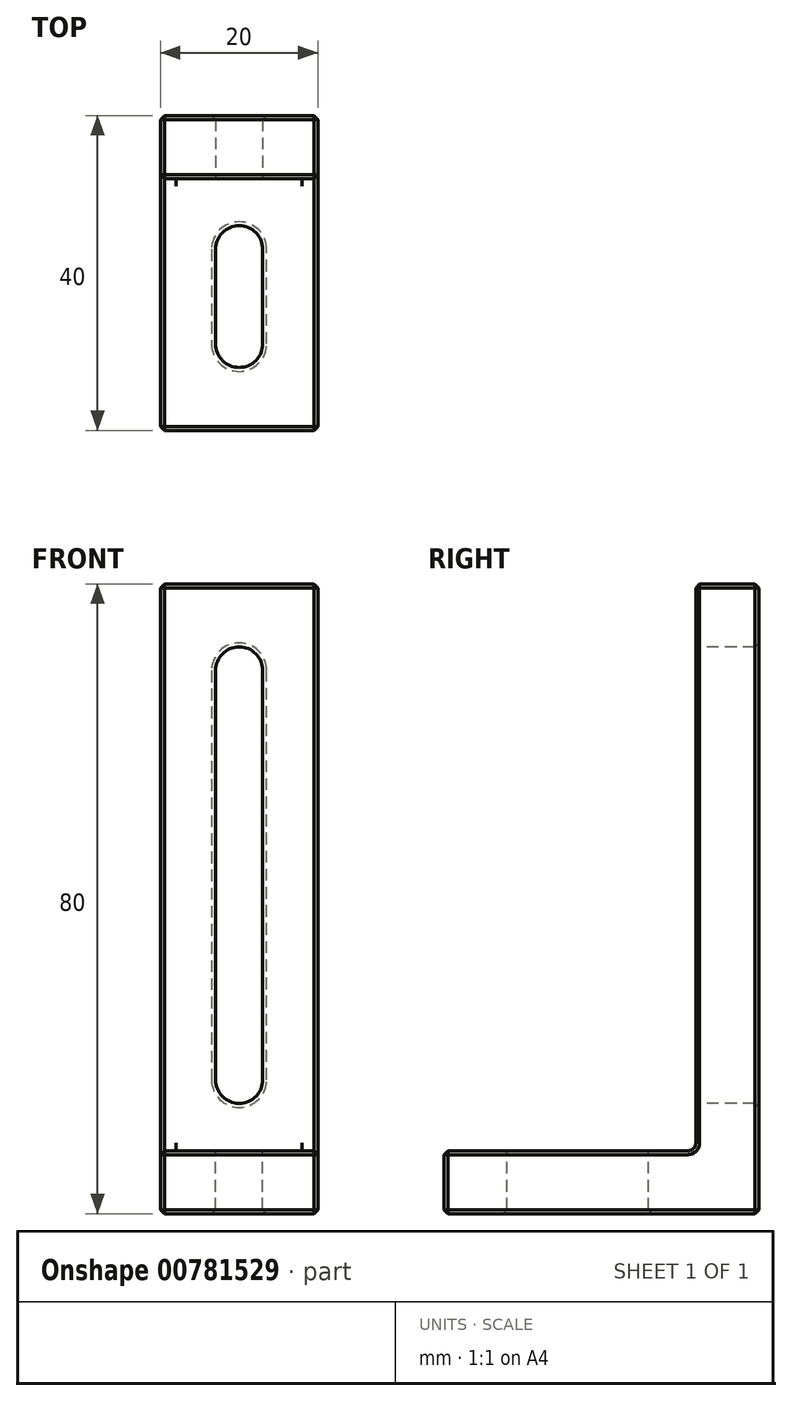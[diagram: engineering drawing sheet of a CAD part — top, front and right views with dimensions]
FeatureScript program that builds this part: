
annotation { "Feature Type Name" : "Feature", "Feature Type Description" : "" }
export const myFeature = defineFeature(function(context is Context, id is Id, definition is map)
    precondition{}
    {
        {
            var Q0;
            Q0=qCreatedBy(makeId("Right.planeOp"),FACE);
            var sketch = newSketch(context, id + "F0", { "sketchPlane" : qUnion([Q0])});
            skLineSegment(sketch, "E0", {"start": v(0, 0) * mm, "end": v(-40, 0) * mm});
            skLineSegment(sketch, "E1", {"start": v(-40, 0) * mm, "end": v(-40, 8) * mm});
            skLineSegment(sketch, "E2", {"start": v(-40, 8) * mm, "end": v(-8, 8) * mm});
            skLineSegment(sketch, "E3", {"start": v(-8, 8) * mm, "end": v(-8, 80) * mm});
            skLineSegment(sketch, "E4", {"start": v(-8, 80) * mm, "end": v(0, 80) * mm});
            skLineSegment(sketch, "E5", {"start": v(0, 80) * mm, "end": v(0, 0) * mm});
            skSolve(sketch);
        }
        {
            var Q0;
            Q0=makeQuery(id+"F0.imprint","IMPRINT",FACE,{"disambiguationData":[TD([[makeQuery(id+"F0.imprint","IMPRINT",EDGE,{"derivedFrom":sQuery(id+"F0.wireOp",EDGE,"E0")}),-1.0]])]});
            extrude(context, id + "F1", {"entities" : qUnion([Q0]), "depth" : 20 * mm, "offsetDistance" : 25 * mm});
        }
        {
            var Q0;
            Q0=makeQuery(id+"F1.opExtrude","SWEPT_EDGE",EDGE,{"disambiguationData":[OSD([sQuery(id+"F0.wireOp",EDGE,"E2"),sQuery(id+"F0.wireOp",EDGE,"E3")])]});
            fillet(context, id + "F2", {"entities" : qUnion([Q0]), "radius" : 1 * mm, "tangentPropagation" : true, "allowEdgeOverflow" : false});
        }
        {
            var Q0;
            Q0=makeQuery(id+"F1.opExtrude","SWEPT_FACE",FACE,{"disambiguationData":[OSD([sQuery(id+"F0.wireOp",EDGE,"E2")])]});
            var sketch = newSketch(context, id + "F3", { "sketchPlane" : qUnion([Q0])});
            skLineSegment(sketch, "E6.bottom", {"start": v(18, -9) * mm, "end": v(2, -9) * mm});
            skLineSegment(sketch, "E6.top", {"start": v(18, -8) * mm, "end": v(2, -8) * mm});
            skLineSegment(sketch, "E6.left", {"start": v(18, -9) * mm, "end": v(18, -8) * mm});
            skLineSegment(sketch, "E6.right", {"start": v(2, -9) * mm, "end": v(2, -8) * mm});
            skSolve(sketch);
        }
        {
            var Q0;
            Q0 = qSketchRegion(id + "F3", true);
            extrude(context, id + "F4", {"entities" : qUnion([Q0]), "operationType" : NewBodyOperationType.REMOVE, "depth" : 25 * mm, "offsetDistance" : 25 * mm});
        }
        {
            var Q0;
            Q0=makeQuery(id+"F4.boolean.opBoolean","MERGE",FACE,{"derivedFrom":[makeQuery(id+"F1.opExtrude","SWEPT_FACE",FACE,{"disambiguationData":[OSD([sQuery(id+"F0.wireOp",EDGE,"E2")])]}),makeQuery(id+"F4.opExtrude","CAP_FACE",FACE,{"disambiguationData":[OSD([sQuery(id+"F3.wireOp",EDGE,"E6.bottom"),sQuery(id+"F3.wireOp",EDGE,"E6.top"),sQuery(id+"F3.wireOp",EDGE,"E6.left"),sQuery(id+"F3.wireOp",EDGE,"E6.right")])],"isStart":true})]});
            var sketch = newSketch(context, id + "F5", { "sketchPlane" : qUnion([Q0])});
            skLineSegment(sketch, "E7", {"start": v(10, 0) * mm, "end": v(10, -40) * mm, "construction": true});
            skArc(sketch, "E8", {"start": v(7, -29) * mm, "mid": v(10, -32) * mm, "end": v(13, -29) * mm});
            skArc(sketch, "E9", {"start": v(13, -17) * mm, "mid": v(10, -14) * mm, "end": v(7, -17) * mm});
            skLineSegment(sketch, "E10", {"start": v(13, -17) * mm, "end": v(13, -29) * mm});
            skLineSegment(sketch, "E11", {"start": v(7, -17) * mm, "end": v(7, -29) * mm});
            skSolve(sketch);
        }
        {
            var Q0;
            Q0 = qSketchRegion(id + "F5", true);
            extrude(context, id + "F6", {"entities" : qUnion([Q0]), "operationType" : NewBodyOperationType.REMOVE, "oppositeDirection" : true, "depth" : 25 * mm, "offsetDistance" : 25 * mm});
        }
        {
            var Q0;
            Q0=makeQuery(id+"F4.boolean.opBoolean","MERGE",FACE,{"derivedFrom":[makeQuery(id+"F1.opExtrude","SWEPT_FACE",FACE,{"disambiguationData":[OSD([sQuery(id+"F0.wireOp",EDGE,"E3")])]}),makeQuery(id+"F4.opExtrude","SWEPT_FACE",FACE,{"disambiguationData":[OSD([sQuery(id+"F3.wireOp",EDGE,"E6.top")])]})]});
            var sketch = newSketch(context, id + "F7", { "sketchPlane" : qUnion([Q0])});
            skLineSegment(sketch, "E12", {"start": v(10, 80) * mm, "end": v(10, 0) * mm});
            skLineSegment(sketch, "E13", {"start": v(13, 69) * mm, "end": v(13, 17) * mm});
            skLineSegment(sketch, "E14", {"start": v(7, 69) * mm, "end": v(7, 17) * mm});
            skArc(sketch, "E15", {"start": v(7, 17) * mm, "mid": v(10, 14) * mm, "end": v(13, 17) * mm});
            skArc(sketch, "E16", {"start": v(13, 69) * mm, "mid": v(10, 72) * mm, "end": v(7, 69) * mm});
            skSolve(sketch);
        }
        {
            var Q0;
            Q0 = qSketchRegion(id + "F7", true);
            extrude(context, id + "F8", {"entities" : qUnion([Q0]), "operationType" : NewBodyOperationType.REMOVE, "oppositeDirection" : true, "depth" : 25 * mm, "offsetDistance" : 25 * mm});
        }
        {
            var Q0;
            Q0=makeQuery(id+"F1.opExtrude","SWEPT_FACE",FACE,{"disambiguationData":[OSD([sQuery(id+"F0.wireOp",EDGE,"E4")])]});
            var Q1;
            Q1=makeQuery(id+"F1.opExtrude","SWEPT_FACE",FACE,{"disambiguationData":[OSD([sQuery(id+"F0.wireOp",EDGE,"E1")])]});
            var Q2;
            Q2=makeQuery(id+"F1.opExtrude","CAP_FACE",FACE,{"disambiguationData":[OSD([sQuery(id+"F0.wireOp",EDGE,"E0"),sQuery(id+"F0.wireOp",EDGE,"E1"),sQuery(id+"F0.wireOp",EDGE,"E2"),sQuery(id+"F0.wireOp",EDGE,"E3"),sQuery(id+"F0.wireOp",EDGE,"E4"),sQuery(id+"F0.wireOp",EDGE,"E5")])],"isStart":false});
            var Q3;
            Q3=makeQuery(id+"F1.opExtrude","CAP_FACE",FACE,{"disambiguationData":[OSD([sQuery(id+"F0.wireOp",EDGE,"E0"),sQuery(id+"F0.wireOp",EDGE,"E1"),sQuery(id+"F0.wireOp",EDGE,"E2"),sQuery(id+"F0.wireOp",EDGE,"E3"),sQuery(id+"F0.wireOp",EDGE,"E4"),sQuery(id+"F0.wireOp",EDGE,"E5")])],"isStart":true});
            var Q4;
            Q4=makeQuery(id+"F8.boolean.opBoolean","COPY",EDGE,{"derivedFrom":makeQuery(id+"F8.opExtrude","CAP_EDGE",EDGE,{"disambiguationData":[OSD([sQuery(id+"F7.wireOp",EDGE,"E14")])],"isStart":true})});
            var Q5;
            Q5=makeQuery(id+"F8.boolean.opBoolean","INTERSECT",EDGE,{"derivedFrom":[makeQuery(id+"F1.opExtrude","SWEPT_FACE",FACE,{"disambiguationData":[OSD([sQuery(id+"F0.wireOp",EDGE,"E5")])]}),makeQuery(id+"F8.opExtrude","SWEPT_FACE",FACE,{"disambiguationData":[OSD([sQuery(id+"F7.wireOp",EDGE,"E14")])]})]});
            var Q6;
            Q6=makeQuery(id+"F6.boolean.opBoolean","INTERSECT",EDGE,{"derivedFrom":[makeQuery(id+"F1.opExtrude","SWEPT_FACE",FACE,{"disambiguationData":[OSD([sQuery(id+"F0.wireOp",EDGE,"E0")])]}),makeQuery(id+"F6.opExtrude","SWEPT_FACE",FACE,{"disambiguationData":[OSD([sQuery(id+"F5.wireOp",EDGE,"E11")])]})]});
            var Q7;
            Q7=makeQuery(id+"F6.boolean.opBoolean","COPY",EDGE,{"derivedFrom":makeQuery(id+"F6.opExtrude","CAP_EDGE",EDGE,{"disambiguationData":[OSD([sQuery(id+"F5.wireOp",EDGE,"E11")])],"isStart":true})});
            var Q8;
            Q8=makeQuery(id+"F1.opExtrude","SWEPT_EDGE",EDGE,{"disambiguationData":[OSD([sQuery(id+"F0.wireOp",EDGE,"E0"),sQuery(id+"F0.wireOp",EDGE,"E5")])]});
            chamfer(context, id + "F9", {"entities" : qUnion([Q0, Q1, Q2, Q3, Q4, Q5, Q6, Q7, Q8]), "width" : 0.5 * mm, "tangentPropagation" : true});
        }
    });
